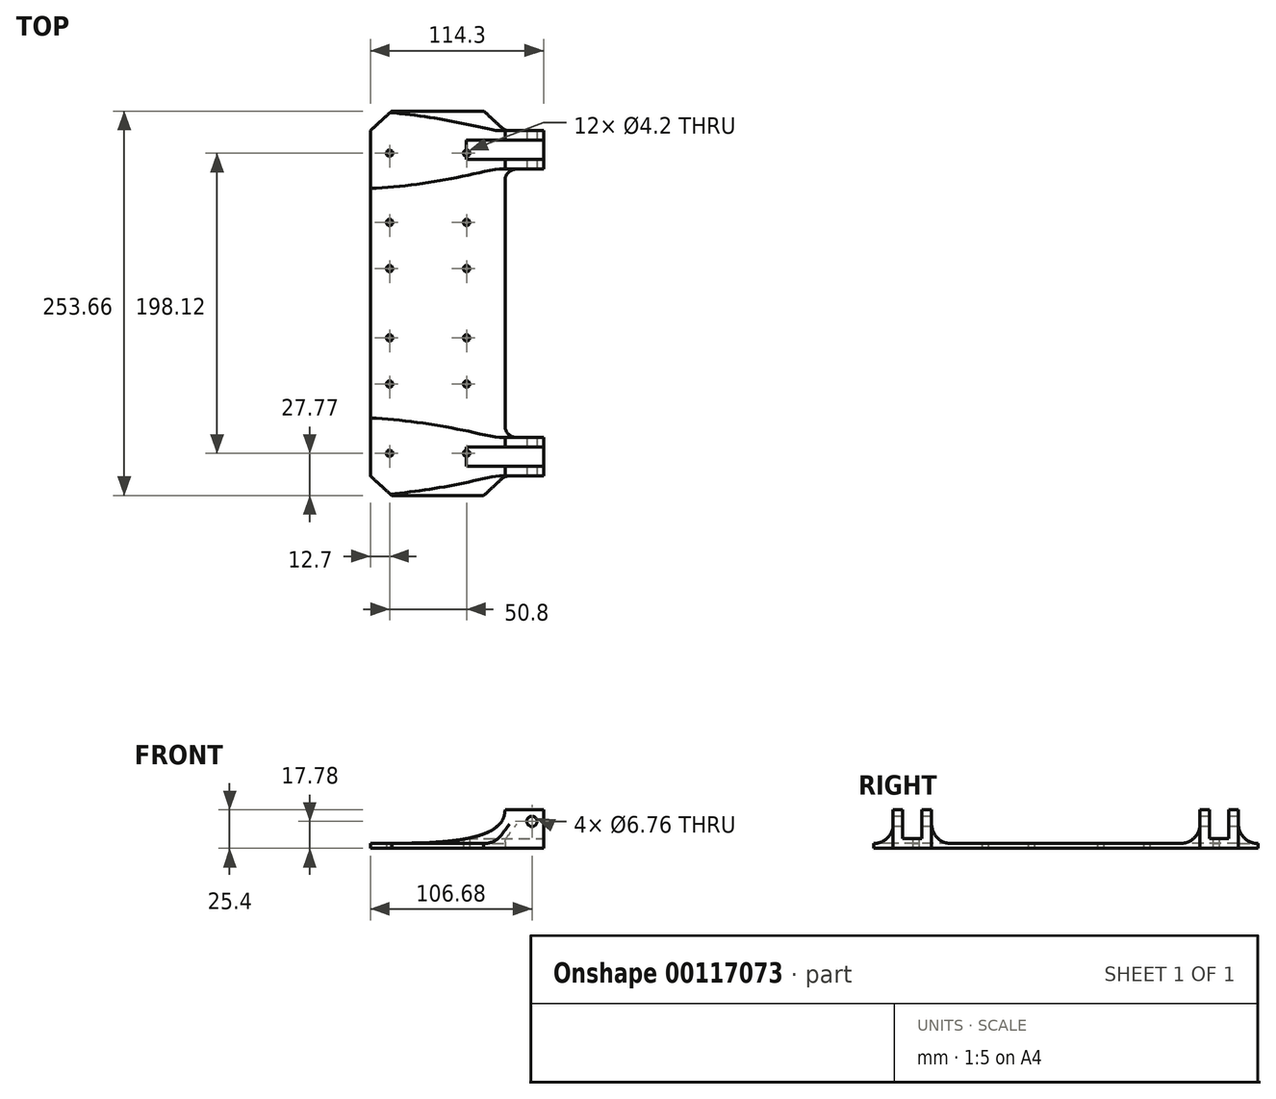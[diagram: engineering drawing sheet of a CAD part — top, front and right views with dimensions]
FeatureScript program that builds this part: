
annotation { "Feature Type Name" : "Feature", "Feature Type Description" : "" }
export const myFeature = defineFeature(function(context is Context, id is Id, definition is map)
    precondition{}
    {
        {
            var Q0;
            Q0=qCreatedBy(makeId("Top.planeOp"),FACE);
            var sketch = newSketch(context, id + "F0", { "sketchPlane" : qUnion([Q0])});
            skLineSegment(sketch, "E0.bottom", {"start": v(76.2, 152.05) * mm, "end": v(50.8, 152.05) * mm});
            skLineSegment(sketch, "E0.top", {"start": v(76.2, 126.65) * mm, "end": v(50.8, 126.65) * mm});
            skLineSegment(sketch, "E0.left", {"start": v(76.2, 152.05) * mm, "end": v(76.2, 126.65) * mm});
            skLineSegment(sketch, "E0.right", {"start": v(50.8, 152.05) * mm, "end": v(50.8, 126.65) * mm});
            skLineSegment(sketch, "E1.bottom", {"start": v(76.2, -50.45) * mm, "end": v(50.8, -50.45) * mm});
            skLineSegment(sketch, "E1.top", {"start": v(76.2, -75.85) * mm, "end": v(50.8, -75.85) * mm});
            skLineSegment(sketch, "E1.left", {"start": v(76.2, -50.45) * mm, "end": v(76.2, -75.85) * mm});
            skLineSegment(sketch, "E1.right", {"start": v(50.8, -50.45) * mm, "end": v(50.8, -75.85) * mm});
            skLineSegment(sketch, "E2", {"start": v(50.8, -50.45) * mm, "end": v(50.8, 126.65) * mm});
            skLineSegment(sketch, "E3", {"start": v(50.8, 152.05) * mm, "end": v(50.8, 177.8) * mm});
            skLineSegment(sketch, "E4", {"start": v(50.8, 177.8) * mm, "end": v(-38.1, 177.8) * mm});
            skLineSegment(sketch, "E5", {"start": v(-38.1, 177.8) * mm, "end": v(-38.1, -101.6) * mm});
            skLineSegment(sketch, "E6", {"start": v(-38.1, -101.6) * mm, "end": v(50.8, -101.6) * mm});
            skLineSegment(sketch, "E7", {"start": v(50.8, -101.6) * mm, "end": v(50.8, -75.85) * mm});
            skLineSegment(sketch, "E8", {"start": v(50.8, 38.1) * mm, "end": v(-38.1, 38.1) * mm});
            skLineSegment(sketch, "E9", {"start": v(50.8, 139.35) * mm, "end": v(76.2, 139.35) * mm});
            skLineSegment(sketch, "E10", {"start": v(50.8, -63.15) * mm, "end": v(76.2, -63.15) * mm});
            skSolve(sketch);
        }
        {
            var Q0;
            Q0=qSketchRegion(id+"F0",true);
            extrude(context, id + "F1", {"entities" : qUnion([Q0]), "depth" : 25.4 * mm});
        }
        {
            var Q0;
            Q0=makeQuery(id+"F1.opExtrude","SWEPT_FACE",FACE,{"disambiguationData":[OSD([sQuery(id+"F0.wireOp",EDGE,"E1.top")])]});
            var sketch = newSketch(context, id + "F2", { "sketchPlane" : qUnion([Q0])});
            skCircle(sketch, "E11", {"center": v(68.58, 17.78) * mm, "radius": 3.38 * mm});
            skSolve(sketch);
        }
        {
            var Q0;
            Q0=qSketchRegion(id+"F2",true);
            extrude(context, id + "F3", {"entities" : qUnion([Q0]), "operationType" : NewBodyOperationType.REMOVE, "endBound" : BoundingType.THROUGH_ALL, "oppositeDirection" : true, "depth" : 177.8 * mm});
        }
        {
            var Q0;
            Q0=makeQuery(id+"F1.opExtrude","SWEPT_FACE",FACE,{"disambiguationData":[OSD([sQuery(id+"F0.wireOp",EDGE,"E0.bottom")])]});
            var sketch = newSketch(context, id + "F4", { "sketchPlane" : qUnion([Q0])});
            skCircle(sketch, "E12", {"center": v(-68.58, 17.78) * mm, "radius": 3.38 * mm});
            skSolve(sketch);
        }
        {
            var Q0;
            Q0=qSketchRegion(id+"F4",true);
            extrude(context, id + "F5", {"entities" : qUnion([Q0]), "operationType" : NewBodyOperationType.REMOVE, "endBound" : BoundingType.THROUGH_ALL, "oppositeDirection" : true, "depth" : 25.4 * mm});
        }
        {
            var Q0;
            Q0=qCreatedBy(makeId("Top.planeOp"),FACE);
            var sketch = newSketch(context, id + "F6", { "sketchPlane" : qUnion([Q0])});
            skPoint(sketch, "E13", {"position": v(25.4, 137.16) * mm});
            skPoint(sketch, "E14", {"position": v(-25.4, 137.16) * mm});
            skPoint(sketch, "E15", {"position": v(25.4, 60.96) * mm});
            skPoint(sketch, "E16", {"position": v(-25.4, 60.96) * mm});
            skPoint(sketch, "E17", {"position": v(25.4, 15.24) * mm});
            skPoint(sketch, "E18", {"position": v(-25.4, 15.24) * mm});
            skPoint(sketch, "E19", {"position": v(25.4, -15.24) * mm});
            skPoint(sketch, "E20", {"position": v(-25.4, -15.24) * mm});
            skPoint(sketch, "E21", {"position": v(25.4, -60.96) * mm});
            skPoint(sketch, "E22", {"position": v(-25.4, -60.96) * mm});
            skPoint(sketch, "E23", {"position": v(25.4, -137.16) * mm});
            skPoint(sketch, "E24", {"position": v(-25.4, -137.16) * mm});
            skPoint(sketch, "E25", {"position": v(25.4, 91.44) * mm});
            skPoint(sketch, "E26", {"position": v(-25.4, 91.44) * mm});
            skSolve(sketch);
        }
        {
            var Q0;
            Q0=sQuery(id+"F6.wireOp",VERTEX,"E24");
            var Q1;
            Q1=sQuery(id+"F6.wireOp",VERTEX,"E23");
            var Q2;
            Q2=sQuery(id+"F6.wireOp",VERTEX,"E22");
            var Q3;
            Q3=sQuery(id+"F6.wireOp",VERTEX,"E21");
            var Q4;
            Q4=sQuery(id+"F6.wireOp",VERTEX,"E20");
            var Q5;
            Q5=sQuery(id+"F6.wireOp",VERTEX,"E19");
            var Q6;
            Q6=sQuery(id+"F6.wireOp",VERTEX,"E17");
            var Q7;
            Q7=sQuery(id+"F6.wireOp",VERTEX,"E18");
            var Q8;
            Q8=sQuery(id+"F6.wireOp",VERTEX,"E16");
            var Q9;
            Q9=sQuery(id+"F6.wireOp",VERTEX,"E15");
            var Q10;
            Q10=sQuery(id+"F6.wireOp",VERTEX,"E13");
            var Q11;
            Q11=sQuery(id+"F6.wireOp",VERTEX,"E14");
            var Q12;
            Q12=sQuery(id+"F6.wireOp",VERTEX,"e64ab47f-2dbb-476e-b239-dff6c19b9388");
            var Q13;
            Q13=sQuery(id+"F6.wireOp",VERTEX,"9fbb3e72-8840-4a96-94a2-e69382cd6c24");
            var Q14;
            Q14=sQuery(id+"F6.wireOp",VERTEX,"E25");
            var Q15;
            Q15=sQuery(id+"F6.wireOp",VERTEX,"E26");
            var Q16;
            Q16=makeQuery(id+"F1.opExtrude","SWEPT_BODY",BODY,{"disambiguationData":[OSD([sQuery(id+"F0.wireOp",EDGE,"E0.bottom"),sQuery(id+"F0.wireOp",EDGE,"E0.top"),sQuery(id+"F0.wireOp",EDGE,"E0.left"),sQuery(id+"F0.wireOp",EDGE,"E1.bottom"),sQuery(id+"F0.wireOp",EDGE,"E1.top"),sQuery(id+"F0.wireOp",EDGE,"E1.left"),sQuery(id+"F0.wireOp",EDGE,"E2"),sQuery(id+"F0.wireOp",EDGE,"E3"),sQuery(id+"F0.wireOp",EDGE,"E4"),sQuery(id+"F0.wireOp",EDGE,"E5"),sQuery(id+"F0.wireOp",EDGE,"E6"),sQuery(id+"F0.wireOp",EDGE,"E7")])]});
            hole(context, id + "F7", {"style" : HoleStyle.SIMPLE, "endStyle" : HoleEndStyle.THROUGH, "oppositeDirection" : true, "standardTappedOrClearance" : lookupTablePath({ "standard" : "ISO", "engagement" : "75%", "pitch" : "0.8 mm", "size" : "M5", "type" : "Tapped" }), "standardBlindInLast" : lookupTablePath({ "standard" : "ISO", "engagement" : "75%", "pitch" : "0.8 mm", "size" : "M5", "type" : "Tapped" }), "holeDiameter" : 4.2 * mm, "startFromSketch" : true, "locations" : qUnion([Q0, Q1, Q2, Q3, Q4, Q5, Q6, Q7, Q8, Q9, Q10, Q11, Q12, Q13, Q14, Q15]), "scope" : qUnion([Q16]), "isTappedThrough" : true, "majorDiameter" : 5 * mm, "showTappedDepth" : true});
        }
        {
            var Q0;
            Q0=makeQuery(id+"F1.opExtrude","SWEPT_FACE",FACE,{"disambiguationData":[OSD([sQuery(id+"F0.wireOp",EDGE,"E6")])]});
            var sketch = newSketch(context, id + "F8", { "sketchPlane" : qUnion([Q0])});
            skFitSpline(sketch, "E27", {"points": [v(50.8, 25.4) * mm, v(-38.1, 3.18) * mm], "startDerivative": vector(0, -66.67) * mm, "endDerivative": vector(-133.35, 0) * mm});
            skPoint(sketch, "E28", {"position": v(6.35, 0) * mm});
            skLineSegment(sketch, "E29", {"start": v(-38.1, 3.18) * mm, "end": v(-38.1, 25.4) * mm});
            skLineSegment(sketch, "E30", {"start": v(-38.1, 25.4) * mm, "end": v(50.8, 25.4) * mm});
            skSolve(sketch);
        }
        {
            var Q0;
            Q0 = qSketchRegion(id + "F8", true);
            extrude(context, id + "F9", {"entities" : qUnion([Q0]), "operationType" : NewBodyOperationType.REMOVE, "endBound" : BoundingType.THROUGH_ALL, "oppositeDirection" : true, "depth" : 25.4 * mm});
        }
        {
            var Q0;
            Q0=makeQuery(id+"F1.opExtrude","SWEPT_FACE",FACE,{"disambiguationData":[OSD([sQuery(id+"F0.wireOp",EDGE,"E1.left")])]});
            var sketch = newSketch(context, id + "F10", { "sketchPlane" : qUnion([Q0])});
            skLineSegment(sketch, "E31.bottom", {"start": v(-69.5, 25.4) * mm, "end": v(-56.8, 25.4) * mm});
            skLineSegment(sketch, "E31.top", {"start": v(-69.5, 6.35) * mm, "end": v(-56.8, 6.35) * mm});
            skLineSegment(sketch, "E31.left", {"start": v(-69.5, 25.4) * mm, "end": v(-69.5, 6.35) * mm});
            skLineSegment(sketch, "E31.right", {"start": v(-56.8, 25.4) * mm, "end": v(-56.8, 6.35) * mm});
            skLineSegment(sketch, "E32.bottom", {"start": v(133, 25.4) * mm, "end": v(145.7, 25.4) * mm});
            skLineSegment(sketch, "E32.top", {"start": v(133, 6.35) * mm, "end": v(145.7, 6.35) * mm});
            skLineSegment(sketch, "E32.left", {"start": v(133, 25.4) * mm, "end": v(133, 6.35) * mm});
            skLineSegment(sketch, "E32.right", {"start": v(145.7, 25.4) * mm, "end": v(145.7, 6.35) * mm});
            skSolve(sketch);
        }
        {
            var Q0;
            Q0 = qSketchRegion(id + "F10", true);
            extrude(context, id + "F11", {"entities" : qUnion([Q0]), "operationType" : NewBodyOperationType.REMOVE, "endBound" : BoundingType.THROUGH_ALL, "oppositeDirection" : true, "offsetDistance" : 25.4 * mm, "depth" : 228.6 * mm});
        }
        {
            var Q0;
            Q0=makeQuery(id+"F1.opExtrude","SWEPT_FACE",FACE,{"disambiguationData":[OSD([sQuery(id+"F0.wireOp",EDGE,"E2")])]});
            var sketch = newSketch(context, id + "F12", { "sketchPlane" : qUnion([Q0])});
            skLineSegment(sketch, "E33.bottom", {"start": v(-50.45, 3.18) * mm, "end": v(126.65, 3.18) * mm});
            skLineSegment(sketch, "E33.top", {"start": v(-50.45, 25.4) * mm, "end": v(126.65, 25.4) * mm});
            skLineSegment(sketch, "E33.left", {"start": v(-50.45, 3.18) * mm, "end": v(-50.45, 25.4) * mm});
            skLineSegment(sketch, "E33.right", {"start": v(126.65, 3.18) * mm, "end": v(126.65, 25.4) * mm});
            skLineSegment(sketch, "E34.bottom", {"start": v(-75.85, 25.4) * mm, "end": v(-101.6, 25.4) * mm});
            skLineSegment(sketch, "E34.top", {"start": v(-75.85, 3.18) * mm, "end": v(-101.6, 3.17) * mm});
            skLineSegment(sketch, "E34.left", {"start": v(-75.85, 25.4) * mm, "end": v(-75.85, 3.18) * mm});
            skLineSegment(sketch, "E34.right", {"start": v(-101.6, 25.4) * mm, "end": v(-101.6, 3.17) * mm});
            skLineSegment(sketch, "E35.bottom", {"start": v(152.05, 25.4) * mm, "end": v(177.8, 25.4) * mm});
            skLineSegment(sketch, "E35.top", {"start": v(152.05, 3.18) * mm, "end": v(177.8, 3.18) * mm});
            skLineSegment(sketch, "E35.left", {"start": v(152.05, 25.4) * mm, "end": v(152.05, 3.18) * mm});
            skLineSegment(sketch, "E35.right", {"start": v(177.8, 25.4) * mm, "end": v(177.8, 3.18) * mm});
            skSolve(sketch);
        }
        {
            var Q0;
            Q0 = qSketchRegion(id + "F12", true);
            extrude(context, id + "F13", {"entities" : qUnion([Q0]), "operationType" : NewBodyOperationType.REMOVE, "endBound" : BoundingType.THROUGH_ALL, "oppositeDirection" : true, "depth" : 25.4 * mm, "offsetDistance" : 25.4 * mm});
        }
        {
            var Q0;
            Q0=makeQuery(id+"F13.boolean.opBoolean","COPY",FACE,{"derivedFrom":makeQuery(id+"F13.opExtrude","SWEPT_FACE",FACE,{"disambiguationData":[OSD([sQuery(id+"F12.wireOp",EDGE,"E34.top")])]})});
            var sketch = newSketch(context, id + "F14", { "sketchPlane" : qUnion([Q0])});
            skLineSegment(sketch, "E36", {"start": v(50.8, -75.85) * mm, "end": v(22.72, -101.6) * mm});
            skLineSegment(sketch, "E37", {"start": v(22.72, -101.6) * mm, "end": v(50.8, -101.6) * mm});
            skLineSegment(sketch, "E38", {"start": v(50.8, -101.6) * mm, "end": v(50.8, -75.85) * mm});
            skLineSegment(sketch, "E39", {"start": v(-38.1, -75.85) * mm, "end": v(-10.02, -101.6) * mm});
            skLineSegment(sketch, "E40", {"start": v(-10.02, -101.6) * mm, "end": v(-38.1, -101.6) * mm});
            skLineSegment(sketch, "E41", {"start": v(-38.1, -101.6) * mm, "end": v(-38.1, -75.85) * mm});
            skSolve(sketch);
        }
        {
            var Q0;
            Q0 = qSketchRegion(id + "F14", true);
            extrude(context, id + "F15", {"entities" : qUnion([Q0]), "operationType" : NewBodyOperationType.REMOVE, "endBound" : BoundingType.THROUGH_ALL, "oppositeDirection" : true, "depth" : 25.4 * mm, "offsetDistance" : 25.4 * mm});
        }
        {
            var Q0;
            Q0=makeQuery(id+"F13.boolean.opBoolean","COPY",FACE,{"derivedFrom":makeQuery(id+"F13.opExtrude","SWEPT_FACE",FACE,{"disambiguationData":[OSD([sQuery(id+"F12.wireOp",EDGE,"E35.top")])]})});
            var sketch = newSketch(context, id + "F16", { "sketchPlane" : qUnion([Q0])});
            skLineSegment(sketch, "E42", {"start": v(50.8, 152.05) * mm, "end": v(50.8, 177.8) * mm});
            skLineSegment(sketch, "E43", {"start": v(50.8, 177.8) * mm, "end": v(22.72, 177.8) * mm});
            skLineSegment(sketch, "E44", {"start": v(22.72, 177.8) * mm, "end": v(50.8, 152.05) * mm});
            skLineSegment(sketch, "E45", {"start": v(-38.1, 152.05) * mm, "end": v(-10.02, 177.8) * mm});
            skLineSegment(sketch, "E46", {"start": v(-10.02, 177.8) * mm, "end": v(-38.1, 177.8) * mm});
            skLineSegment(sketch, "E47", {"start": v(-38.1, 177.8) * mm, "end": v(-38.1, 152.05) * mm});
            skSolve(sketch);
        }
        {
            var Q0;
            Q0 = qSketchRegion(id + "F16", true);
            extrude(context, id + "F17", {"entities" : qUnion([Q0]), "operationType" : NewBodyOperationType.REMOVE, "endBound" : BoundingType.THROUGH_ALL, "oppositeDirection" : true, "depth" : 25.4 * mm, "offsetDistance" : 25.4 * mm});
        }
        {
            var Q0;
            Q0=makeQuery(id+"F1.opExtrude","CAP_FACE",FACE,{"disambiguationData":[OSD([sQuery(id+"F0.wireOp",EDGE,"E0.bottom"),sQuery(id+"F0.wireOp",EDGE,"E0.top"),sQuery(id+"F0.wireOp",EDGE,"E0.left"),sQuery(id+"F0.wireOp",EDGE,"E1.bottom"),sQuery(id+"F0.wireOp",EDGE,"E1.top"),sQuery(id+"F0.wireOp",EDGE,"E1.left"),sQuery(id+"F0.wireOp",EDGE,"E2"),sQuery(id+"F0.wireOp",EDGE,"E3"),sQuery(id+"F0.wireOp",EDGE,"E4"),sQuery(id+"F0.wireOp",EDGE,"E5"),sQuery(id+"F0.wireOp",EDGE,"E6"),sQuery(id+"F0.wireOp",EDGE,"E7")])],"isStart":true});
            var sketch = newSketch(context, id + "F18", { "sketchPlane" : qUnion([Q0])});
            skLineSegment(sketch, "E48", {"start": v(-24.06, 88.73) * mm, "end": v(36.76, 88.73) * mm});
            skLineSegment(sketch, "E49", {"start": v(36.76, 88.73) * mm, "end": v(22.72, 101.6) * mm});
            skLineSegment(sketch, "E50", {"start": v(22.72, 101.6) * mm, "end": v(-10.02, 101.6) * mm});
            skLineSegment(sketch, "E51", {"start": v(-10.02, 101.6) * mm, "end": v(-24.06, 88.73) * mm});
            skLineSegment(sketch, "E52", {"start": v(-24.06, -164.93) * mm, "end": v(36.76, -164.92) * mm});
            skLineSegment(sketch, "E53", {"start": v(36.76, -164.92) * mm, "end": v(22.72, -177.8) * mm});
            skLineSegment(sketch, "E54", {"start": v(22.72, -177.8) * mm, "end": v(-10.02, -177.8) * mm});
            skLineSegment(sketch, "E55", {"start": v(-10.02, -177.8) * mm, "end": v(-24.06, -164.93) * mm});
            skSolve(sketch);
        }
        {
            var Q0;
            Q0 = qSketchRegion(id + "F18", true);
            extrude(context, id + "F19", {"entities" : qUnion([Q0]), "operationType" : NewBodyOperationType.REMOVE, "endBound" : BoundingType.THROUGH_ALL, "oppositeDirection" : true, "depth" : 25.4 * mm, "offsetDistance" : 25.4 * mm});
        }
        {
            var Q0;
            Q0=makeQuery(id+"F13.boolean.opBoolean","COPY",EDGE,{"derivedFrom":makeQuery(id+"F13.opExtrude","SWEPT_EDGE",EDGE,{"disambiguationData":[OSD([sQuery(id+"F0.wireOp",EDGE,"E1.bottom"),sQuery(id+"F0.wireOp",EDGE,"E1.right"),sQuery(id+"F0.wireOp",EDGE,"E2"),sQuery(id+"F12.wireOp",EDGE,"E33.bottom"),sQuery(id+"F12.wireOp",EDGE,"E33.left")])]})});
            var Q1;
            Q1=makeQuery(id+"F13.boolean.opBoolean","COPY",EDGE,{"derivedFrom":makeQuery(id+"F13.opExtrude","SWEPT_EDGE",EDGE,{"disambiguationData":[OSD([sQuery(id+"F12.wireOp",EDGE,"E34.top"),sQuery(id+"F12.wireOp",EDGE,"E34.left")])]})});
            var Q2;
            Q2=makeQuery(id+"F13.boolean.opBoolean","COPY",EDGE,{"derivedFrom":makeQuery(id+"F13.opExtrude","SWEPT_EDGE",EDGE,{"disambiguationData":[OSD([sQuery(id+"F12.wireOp",EDGE,"E35.top"),sQuery(id+"F12.wireOp",EDGE,"E35.left")])]})});
            var Q3;
            Q3=makeQuery(id+"F13.boolean.opBoolean","COPY",EDGE,{"derivedFrom":makeQuery(id+"F13.opExtrude","SWEPT_EDGE",EDGE,{"disambiguationData":[OSD([sQuery(id+"F0.wireOp",EDGE,"E0.top"),sQuery(id+"F0.wireOp",EDGE,"E0.right"),sQuery(id+"F0.wireOp",EDGE,"E2"),sQuery(id+"F12.wireOp",EDGE,"E33.bottom"),sQuery(id+"F12.wireOp",EDGE,"E33.right")])]})});
            fillet(context, id + "F20", {"entities" : qUnion([Q0, Q1, Q2, Q3]), "tangentPropagation" : true, "radius" : 12.7 * mm, "defaultsChanged" : true, "vertexSettings" : [], "allowEdgeOverflow" : false});
        }
        {
            var Q0;
            Q0=makeQuery(id+"F15.boolean.opBoolean","MERGE",EDGE,{"derivedFrom":[makeQuery(id+"F1.opExtrude","SWEPT_EDGE",EDGE,{"disambiguationData":[OSD([sQuery(id+"F0.wireOp",EDGE,"E1.top"),sQuery(id+"F0.wireOp",EDGE,"E1.right"),sQuery(id+"F0.wireOp",EDGE,"E7")])]})],"fromTools":[makeQuery(id+"F15.opExtrude","SWEPT_EDGE",EDGE,{"disambiguationData":[OSD([sQuery(id+"F12.wireOp",EDGE,"E34.top"),sQuery(id+"F12.wireOp",EDGE,"E34.left"),sQuery(id+"F14.wireOp",EDGE,"E36"),sQuery(id+"F14.wireOp",EDGE,"E38")])]})]});
            var Q1;
            Q1=makeQuery(id+"F17.boolean.opBoolean","MERGE",EDGE,{"derivedFrom":[makeQuery(id+"F1.opExtrude","SWEPT_EDGE",EDGE,{"disambiguationData":[OSD([sQuery(id+"F0.wireOp",EDGE,"E0.bottom"),sQuery(id+"F0.wireOp",EDGE,"E0.right"),sQuery(id+"F0.wireOp",EDGE,"E3")])]})],"fromTools":[makeQuery(id+"F17.opExtrude","SWEPT_EDGE",EDGE,{"disambiguationData":[OSD([sQuery(id+"F12.wireOp",EDGE,"E35.top"),sQuery(id+"F12.wireOp",EDGE,"E35.left"),sQuery(id+"F16.wireOp",EDGE,"E42"),sQuery(id+"F16.wireOp",EDGE,"E44")])]})]});
            var Q2;
            Q2=makeQuery(id+"F1.opExtrude","SWEPT_EDGE",EDGE,{"disambiguationData":[OSD([sQuery(id+"F0.wireOp",EDGE,"E1.bottom"),sQuery(id+"F0.wireOp",EDGE,"E1.right"),sQuery(id+"F0.wireOp",EDGE,"E2")])]});
            var Q3;
            Q3=makeQuery(id+"F1.opExtrude","SWEPT_EDGE",EDGE,{"disambiguationData":[OSD([sQuery(id+"F0.wireOp",EDGE,"E0.top"),sQuery(id+"F0.wireOp",EDGE,"E0.right"),sQuery(id+"F0.wireOp",EDGE,"E2")])]});
            fillet(context, id + "F21", {"entities" : qUnion([Q0, Q1, Q2, Q3]), "tangentPropagation" : true, "radius" : 7.62 * mm, "defaultsChanged" : true, "vertexSettings" : [], "allowEdgeOverflow" : false});
        }
        {
            var Q0;
            Q0=makeQuery(id+"F1.opExtrude","SWEPT_BODY",BODY,{"disambiguationData":[OSD([sQuery(id+"F0.wireOp",EDGE,"E0.bottom"),sQuery(id+"F0.wireOp",EDGE,"E0.top"),sQuery(id+"F0.wireOp",EDGE,"E0.left"),sQuery(id+"F0.wireOp",EDGE,"E1.bottom"),sQuery(id+"F0.wireOp",EDGE,"E1.top"),sQuery(id+"F0.wireOp",EDGE,"E1.left"),sQuery(id+"F0.wireOp",EDGE,"E2"),sQuery(id+"F0.wireOp",EDGE,"E3"),sQuery(id+"F0.wireOp",EDGE,"E4"),sQuery(id+"F0.wireOp",EDGE,"E5"),sQuery(id+"F0.wireOp",EDGE,"E6"),sQuery(id+"F0.wireOp",EDGE,"E7")])]});
            transform(context, id + "F22", {"entities" : qUnion([Q0]), "transformType" : TransformType.TRANSLATION_3D, "dx" : 0 * mm, "dy" : 0 * mm, "dz" : 0 * mm, "makeCopy" : true});
        }
        {
            var Q0;
            Q0=makeQuery(id+"F22.opPattern","COPY",BODY,{"derivedFrom":makeQuery(id+"F1.opExtrude","SWEPT_BODY",BODY,{"disambiguationData":[OSD([sQuery(id+"F0.wireOp",EDGE,"E0.bottom"),sQuery(id+"F0.wireOp",EDGE,"E0.top"),sQuery(id+"F0.wireOp",EDGE,"E0.left"),sQuery(id+"F0.wireOp",EDGE,"E1.bottom"),sQuery(id+"F0.wireOp",EDGE,"E1.top"),sQuery(id+"F0.wireOp",EDGE,"E1.left"),sQuery(id+"F0.wireOp",EDGE,"E2"),sQuery(id+"F0.wireOp",EDGE,"E3"),sQuery(id+"F0.wireOp",EDGE,"E4"),sQuery(id+"F0.wireOp",EDGE,"E5"),sQuery(id+"F0.wireOp",EDGE,"E6"),sQuery(id+"F0.wireOp",EDGE,"E7")])]}),"instanceName":"1"});
            deleteBodies(context, id + "F23", {"entities" : qUnion([Q0])});
        }
    });
